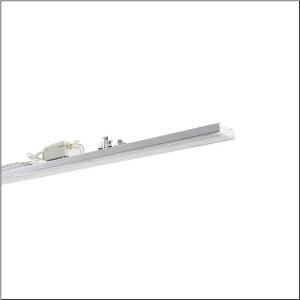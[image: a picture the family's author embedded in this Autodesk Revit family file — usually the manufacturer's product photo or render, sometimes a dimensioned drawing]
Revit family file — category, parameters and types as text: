
# Revit family: licross_r__11_recessed_ho_51tl12dn4exm3c_4ac0
name_source: partatom
category: Lighting Fixtures
units: mm (PartAtom-declared; Revit-internal decimal feet)

## family parameters
Cut with Voids When Loaded = No
Host = Face
Light Source = No
Part Type = Normal
Room Calculation Point = No
Round Connector Dimension = Use Diameter
Shared = No

## types (1)
- --- (1 x LED, 1000 lm, 7.2 W, 4000K)
    Apparent Load = 7 VA
    CIE Flux Codes = 66 91 98 100 100
    Color Rendering = 80
    Color Temperature = 4000K
    Default Elevation = 1800 mm
    Description = Licross® 11 Recessed HO, luminaire insert, of sheet steel, coil coated, white, length: 1.500mm, width: 66mm, height: 67mm, LED rated luminous flux: 14.030lm, light colour: 840, SDCM (Standard Deviation of Colour Matching)MacAdam ≤ 2 SDCM (initial), control gear: DALI 2 (for two DALI lines), with plug, 6-pole, with phase selection, for trunking rail, 14-core, mains connection: 220..240V, AC, 50/60Hz, rated input power: 81W, for trunking rail, 14-core, internal wiring halogen-free, for emergency light function, converter,control gear: single battery element, battery: LiFePO4, 9Ah, primary optical cover: cover, of PMMA, light emission: direct distribution, primary light characteristic: symmetric, protection rating (complete): IP40, insulation class (complete): insulation class I (protective earthing), certification: CE, UKCA, protection symbol: D if used in an environment without relevant dust loads with corresponding accessories, impact resistance: IK06, permissible ambient temperature for indoor applications: +5..+30°C, standard: EN 60598-2-22, LABS conformity tested according to VDMA 24364:2018-05, reducing of maximum allowable ambient temperature of 5°C with ceiling mounting, corresponds to IFS (International Featured Standards) requirements for safety and quality in the food industry, packaging unit: 1 piece
    Height = 58 mm
    Lamp = 1 x LED
    Lamp Light Flux = 1000 lm
    Lamp Power = 7.2 W
    Lamp count = 1
    Length = 1500 mm
    Luminous efficacy = 139 lm/W
    Manufacturer = Siteco
    ModVariant = No
    Model = 51TL12DN4EXM3C
    Mounting Place = Ceiling
    Mounting Type = Pendant
    Number of Poles = 1
    OnlyDefault = Yes
    Power Factor = 1
    Product Name = Licross® 11 Recessed HO
    Product group = luminaire insert | ceiling pendant
    ProductGroupID = 901
    Protection Class = Protection class I
    Protection Degree = IP 40
    RLX_Detail_Level = 1
    RLX_Emergency_Light_Flux = 0 lm
    RLX_Emergency_Type = 0
    RLX_Emergency_Type_DB = No
    RlxData = <blob elided: 25077 chars, md5=169e8cbb>
    Socket = socket
    Standby Power = 0 W
    System Light Flux = 1000 lm
    System Power = 7 W
    Type Comments = : emergency light operation: 3 h
    Type Image = l_1296930.jpg
    URL = http://relux.com
    VarID = @adj_097757
    Voltage = 0 V
    Weight = 0.00 kg
    Width = 66 mm

## geometry (parser evidence)
native form markers: Blend x4, Sweep x11
no freeform markers — native parametric forms only
